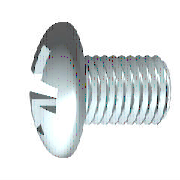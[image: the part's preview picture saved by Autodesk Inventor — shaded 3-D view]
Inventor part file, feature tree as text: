
AUTODESK INVENTOR PART (.ipt)
format: ipt  version: 2020 (Build 240168000, 168)  size: 279,040 bytes
history: native  units: mm (DEFAULTED — no unit token found)
features: extrude x1, other x1, plane x1
ambient origin geometry x7: Origin, YZ Plane, XZ Plane, X Axis, Y Axis, Z Axis, Center Point
bodies: Solid1 (feature_tree), Body (feature_tree)
feature tree (3):
  extrude  "Slot"  Depth=2.0mm
  other  "Cut"
  plane  "Work Plane3"
